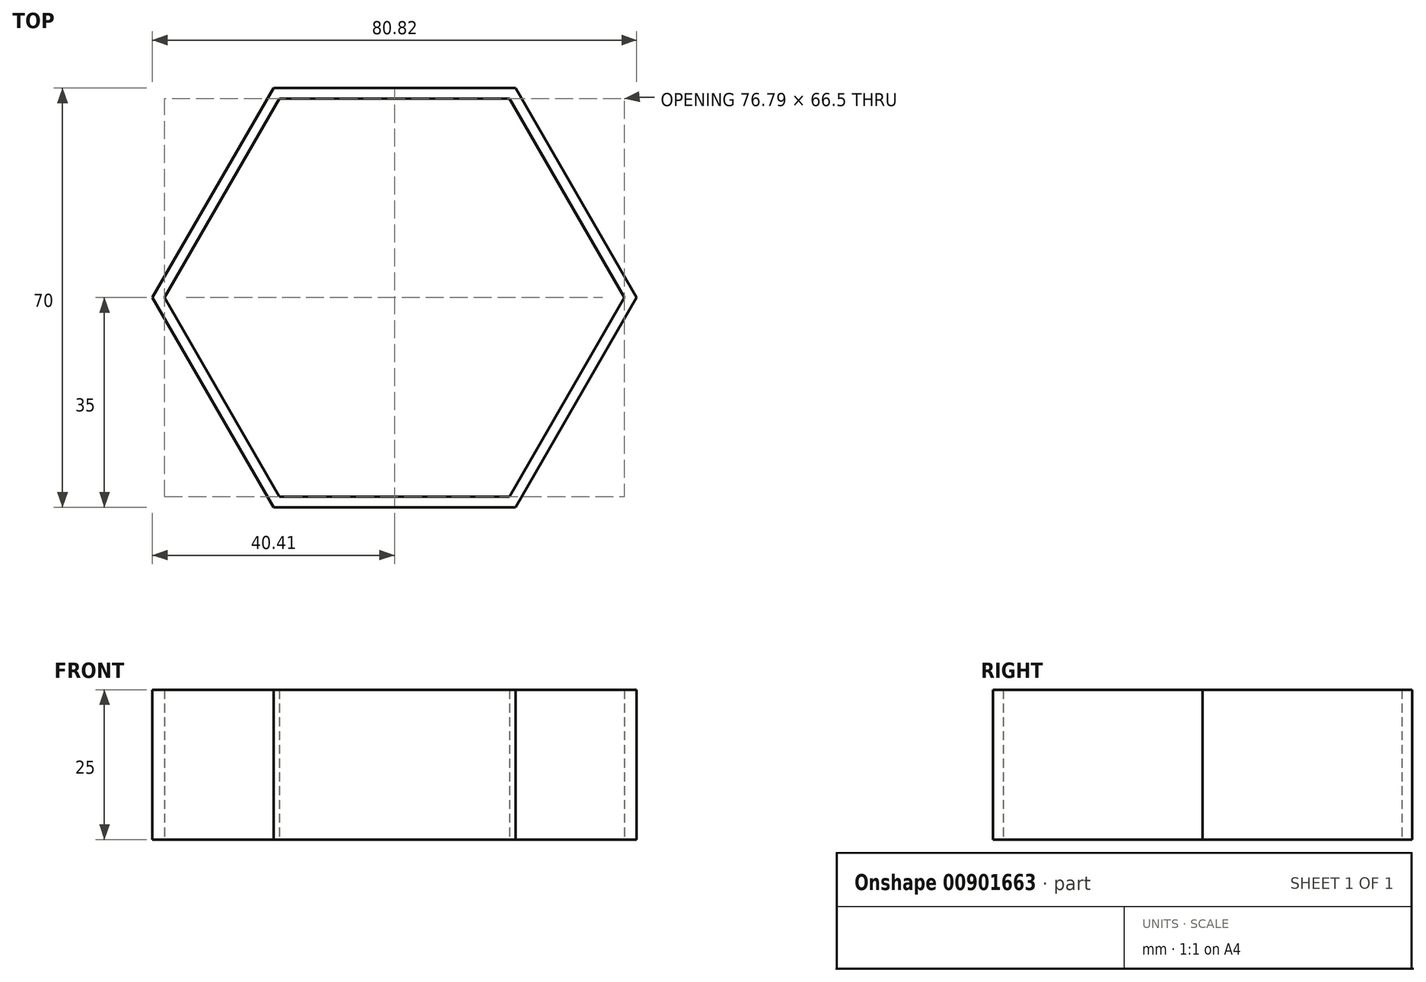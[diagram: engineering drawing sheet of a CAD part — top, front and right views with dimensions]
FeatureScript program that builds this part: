
annotation { "Feature Type Name" : "Feature", "Feature Type Description" : "" }
export const myFeature = defineFeature(function(context is Context, id is Id, definition is map)
    precondition{}
    {
        {
            var Q0;
            Q0=qCreatedBy(makeId("Top.planeOp"),FACE);
            var sketch = newSketch(context, id + "F0", { "sketchPlane" : qUnion([Q0])});
            skCircle(sketch, "E0.cCircle", {"center": v(0, 0) * mm, "radius": 33.25 * mm, "construction": true});
            skLineSegment(sketch, "E0.0", {"start": v(38.4, 0) * mm, "end": v(19.2, -33.25) * mm});
            skLineSegment(sketch, "E0.1", {"start": v(19.2, -33.25) * mm, "end": v(-19.2, -33.25) * mm});
            skLineSegment(sketch, "E0.2", {"start": v(-19.2, -33.25) * mm, "end": v(-38.4, 0) * mm});
            skLineSegment(sketch, "E0.3", {"start": v(-38.4, 0) * mm, "end": v(-19.2, 33.25) * mm});
            skLineSegment(sketch, "E0.4", {"start": v(-19.2, 33.25) * mm, "end": v(19.2, 33.25) * mm});
            skLineSegment(sketch, "E0.5", {"start": v(19.2, 33.25) * mm, "end": v(38.4, 0) * mm});
            skPoint(sketch, "E0.0.midPoint", {"position": v(28.8, -16.63) * mm});
            skCircle(sketch, "E1.cCircle", {"center": v(0, 0) * mm, "radius": 35 * mm, "construction": true});
            skLineSegment(sketch, "E1.0", {"start": v(40.41, 0) * mm, "end": v(20.2, -35) * mm});
            skLineSegment(sketch, "E1.1", {"start": v(20.2, -35) * mm, "end": v(-20.2, -35) * mm});
            skLineSegment(sketch, "E1.2", {"start": v(-20.2, -35) * mm, "end": v(-40.41, 0) * mm});
            skLineSegment(sketch, "E1.3", {"start": v(-40.41, 0) * mm, "end": v(-20.2, 35) * mm});
            skLineSegment(sketch, "E1.4", {"start": v(-20.2, 35) * mm, "end": v(20.2, 35) * mm});
            skLineSegment(sketch, "E1.5", {"start": v(20.2, 35) * mm, "end": v(40.41, 0) * mm});
            skPoint(sketch, "E1.0.midPoint", {"position": v(30.31, -17.5) * mm});
            skSolve(sketch);
        }
        {
            var Q0;
            Q0=makeQuery(id+"F0.imprint","IMPRINT",FACE,{"disambiguationData":[TD([[makeQuery(id+"F0.imprint","IMPRINT",EDGE,{"derivedFrom":sQuery(id+"F0.wireOp",EDGE,"E0.0")}),1.0]])]});
            extrude(context, id + "F1", {"entities" : qUnion([Q0]), "depth" : 25 * mm, "offsetDistance" : 25 * mm});
        }
    });
